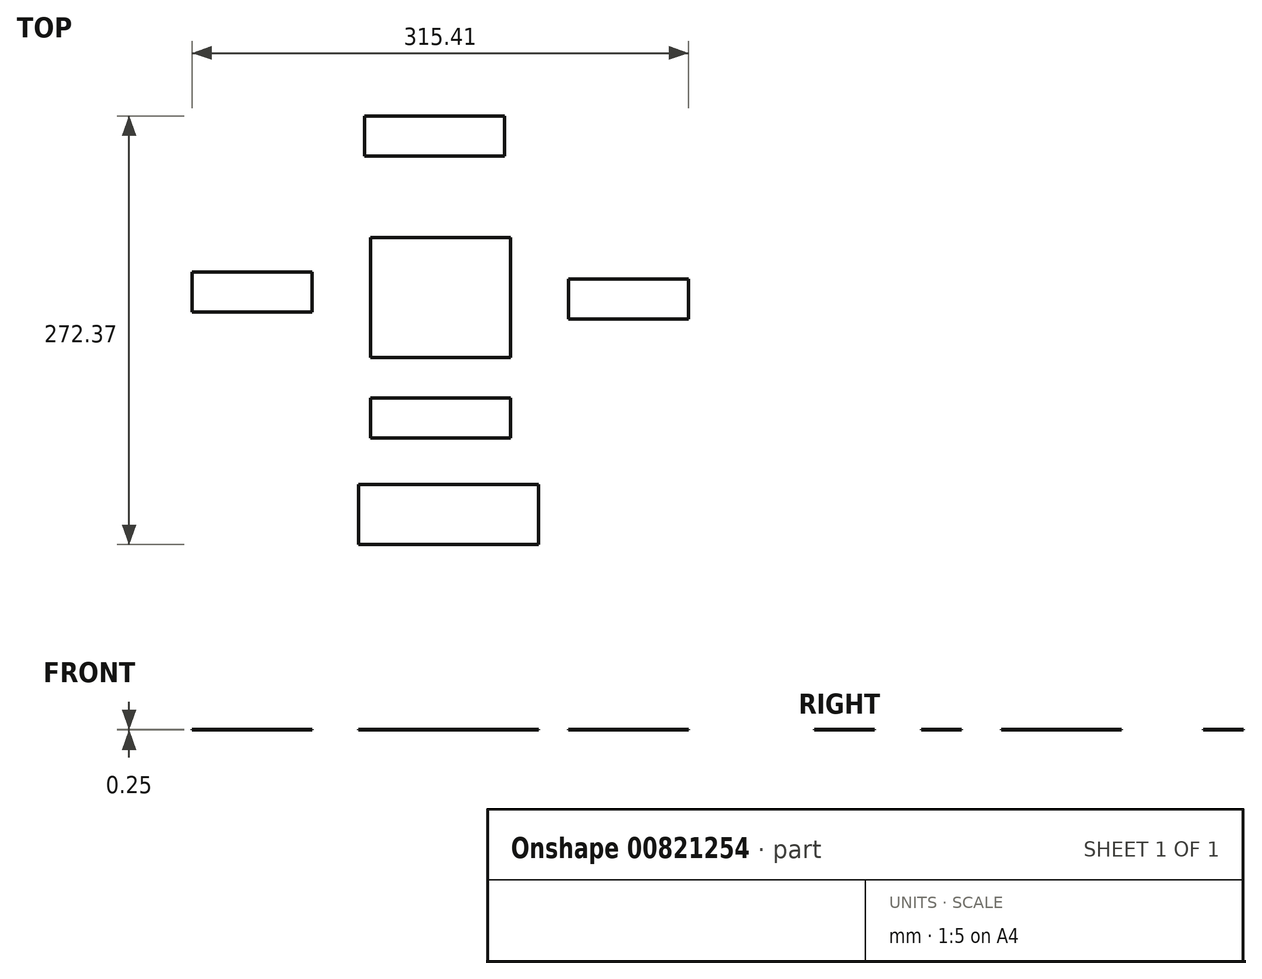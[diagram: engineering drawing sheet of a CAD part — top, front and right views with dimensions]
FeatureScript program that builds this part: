
annotation { "Feature Type Name" : "Feature", "Feature Type Description" : "" }
export const myFeature = defineFeature(function(context is Context, id is Id, definition is map)
    precondition{}
    {
        {
            assignVariable(context, id + "F0", {"name" : "th", "anyValue" : .25});
        }
        {
            var Q0;
            Q0=qCreatedBy(makeId("Top.planeOp"),FACE);
            var sketch = newSketch(context, id + "F1", { "sketchPlane" : qUnion([Q0])});
            skLineSegment(sketch, "E0.bottom", {"start": v(-290.17, 54.38) * mm, "end": v(-213.97, 54.38) * mm});
            skLineSegment(sketch, "E0.top", {"start": v(-290.17, 28.98) * mm, "end": v(-213.97, 28.98) * mm});
            skLineSegment(sketch, "E0.left", {"start": v(-290.17, 54.38) * mm, "end": v(-290.17, 28.98) * mm});
            skLineSegment(sketch, "E0.right", {"start": v(-213.97, 54.38) * mm, "end": v(-213.97, 28.98) * mm});
            skLineSegment(sketch, "E1.bottom", {"start": v(-176.66, 76.2) * mm, "end": v(-87.76, 76.2) * mm});
            skLineSegment(sketch, "E1.top", {"start": v(-176.66, 0) * mm, "end": v(-87.76, 0) * mm});
            skLineSegment(sketch, "E1.left", {"start": v(-176.66, 76.2) * mm, "end": v(-176.66, 0) * mm});
            skLineSegment(sketch, "E1.right", {"start": v(-87.76, 76.2) * mm, "end": v(-87.76, 0) * mm});
            skLineSegment(sketch, "E2.bottom", {"start": v(-180.74, 153.55) * mm, "end": v(-91.84, 153.55) * mm});
            skLineSegment(sketch, "E2.top", {"start": v(-180.74, 128.15) * mm, "end": v(-91.84, 128.15) * mm});
            skLineSegment(sketch, "E2.left", {"start": v(-180.74, 153.55) * mm, "end": v(-180.74, 128.15) * mm});
            skLineSegment(sketch, "E2.right", {"start": v(-91.84, 153.55) * mm, "end": v(-91.84, 128.15) * mm});
            skLineSegment(sketch, "E3.bottom", {"start": v(-184.28, -80.72) * mm, "end": v(-69.98, -80.72) * mm});
            skLineSegment(sketch, "E3.top", {"start": v(-184.28, -118.82) * mm, "end": v(-69.98, -118.82) * mm});
            skLineSegment(sketch, "E3.left", {"start": v(-184.28, -80.72) * mm, "end": v(-184.28, -118.82) * mm});
            skLineSegment(sketch, "E3.right", {"start": v(-69.98, -80.72) * mm, "end": v(-69.98, -118.82) * mm});
            skLineSegment(sketch, "E4.bottom", {"start": v(-176.66, -25.61) * mm, "end": v(-87.76, -25.61) * mm});
            skLineSegment(sketch, "E4.top", {"start": v(-176.66, -51.01) * mm, "end": v(-87.76, -51.01) * mm});
            skLineSegment(sketch, "E4.left", {"start": v(-176.66, -25.61) * mm, "end": v(-176.66, -51.01) * mm});
            skLineSegment(sketch, "E4.right", {"start": v(-87.76, -25.61) * mm, "end": v(-87.76, -51.01) * mm});
            skLineSegment(sketch, "E5.bottom", {"start": v(-50.96, 49.8) * mm, "end": v(25.24, 49.8) * mm});
            skLineSegment(sketch, "E5.top", {"start": v(-50.96, 24.4) * mm, "end": v(25.24, 24.4) * mm});
            skLineSegment(sketch, "E5.left", {"start": v(-50.96, 49.8) * mm, "end": v(-50.96, 24.4) * mm});
            skLineSegment(sketch, "E5.right", {"start": v(25.24, 49.8) * mm, "end": v(25.24, 24.4) * mm});
            skSolve(sketch);
        }
        {
            var Q0;
            Q0 = qSketchRegion(id + "F1", true);
            extrude(context, id + "F2", {"entities" : qUnion([Q0]), "depth" : (getVariable(context, 'th')) * mm, "offsetDistance" : 25.4 * mm});
        }
    });
